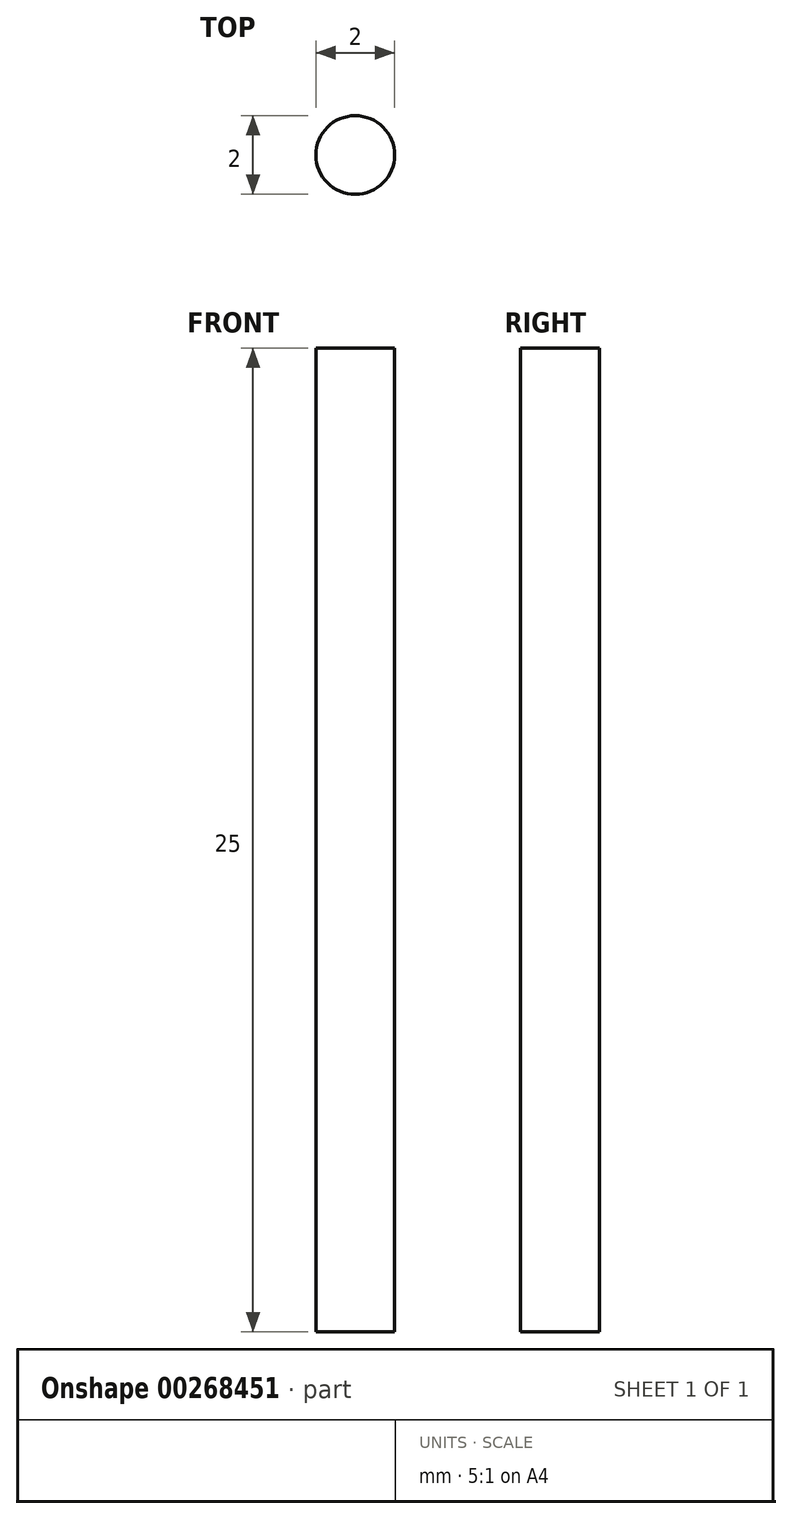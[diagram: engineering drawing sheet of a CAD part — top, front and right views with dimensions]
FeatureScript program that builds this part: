
annotation { "Feature Type Name" : "Feature", "Feature Type Description" : "" }
export const myFeature = defineFeature(function(context is Context, id is Id, definition is map)
    precondition{}
    {
        {
            var Q0;
            Q0=qCreatedBy(makeId("Top.planeOp"),FACE);
            var sketch = newSketch(context, id + "F0", { "sketchPlane" : qUnion([Q0])});
            skCircle(sketch, "E0", {"center": v(0, 0) * mm, "radius": 1 * mm});
            skSolve(sketch);
        }
        {
            var Q0;
            Q0 = qSketchRegion(id + "F0", true);
            extrude(context, id + "F1", {"entities" : qUnion([Q0]), "depth" : 25 * mm, "offsetDistance" : 25 * mm});
        }
    });
